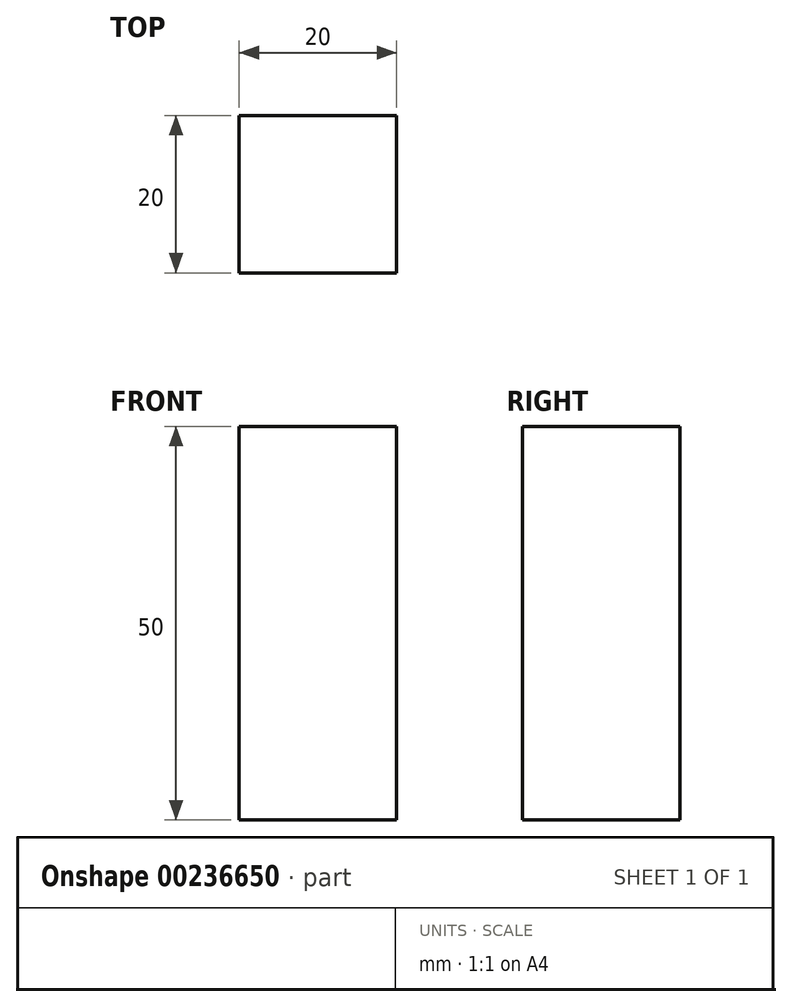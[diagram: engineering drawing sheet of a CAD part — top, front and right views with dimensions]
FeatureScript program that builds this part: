
annotation { "Feature Type Name" : "Feature", "Feature Type Description" : "" }
export const myFeature = defineFeature(function(context is Context, id is Id, definition is map)
    precondition{}
    {
        {
            var Q0;
            Q0=qCreatedBy(makeId("Top.planeOp"),FACE);
            var sketch = newSketch(context, id + "F0", { "sketchPlane" : qUnion([Q0])});
            skLineSegment(sketch, "E0.bottom", {"start": v(-1.93, 1.53) * mm, "end": v(18.07, 1.53) * mm});
            skLineSegment(sketch, "E0.top", {"start": v(-1.93, -18.47) * mm, "end": v(18.07, -18.47) * mm});
            skLineSegment(sketch, "E0.left", {"start": v(-1.93, 1.53) * mm, "end": v(-1.93, -18.47) * mm});
            skLineSegment(sketch, "E0.right", {"start": v(18.07, 1.53) * mm, "end": v(18.07, -18.47) * mm});
            skSolve(sketch);
        }
        {
            var Q0;
            Q0=makeQuery(id+"F0.imprint","IMPRINT",FACE,{"disambiguationData":[TD([[makeQuery(id+"F0.imprint","IMPRINT",EDGE,{"derivedFrom":sQuery(id+"F0.wireOp",EDGE,"E0.bottom")}),-1.0]])]});
            extrude(context, id + "F1", {"entities" : qUnion([Q0]), "depth" : 50 * mm});
        }
    });
